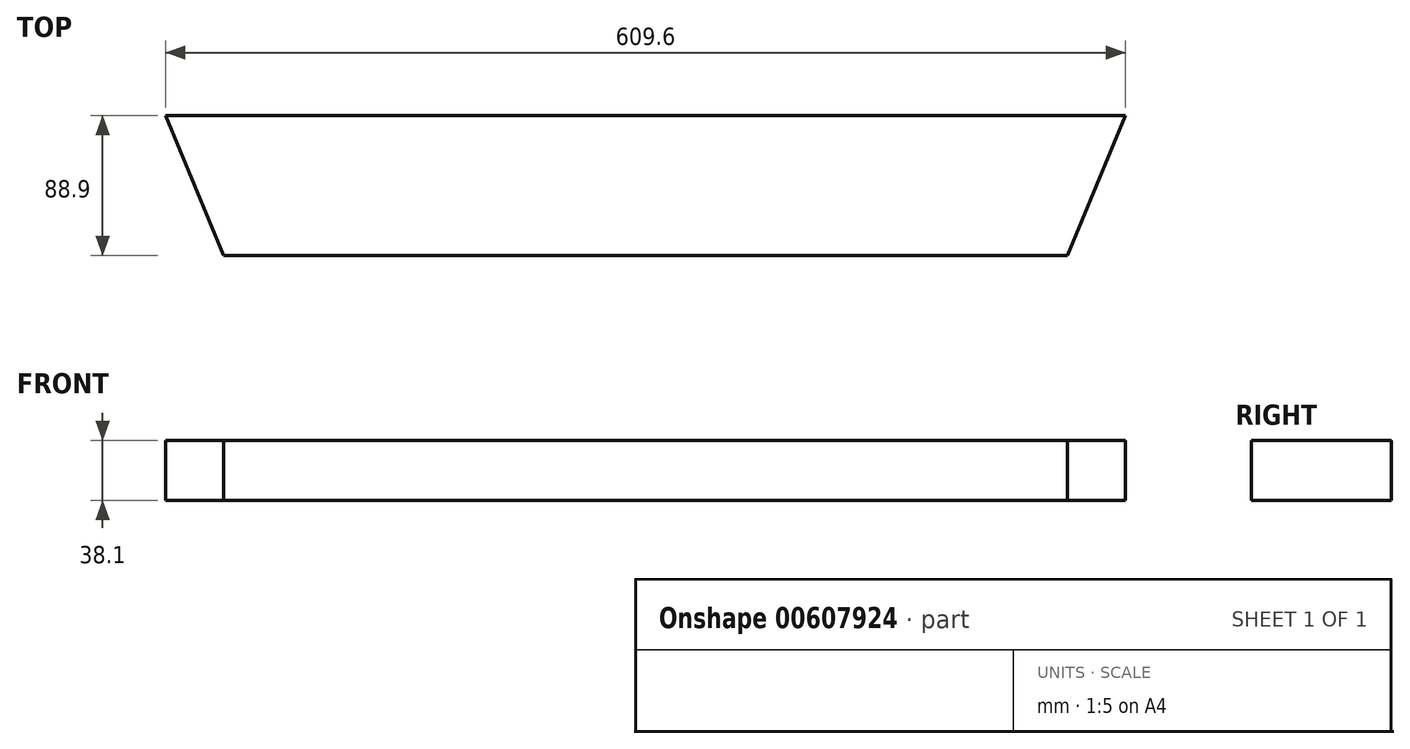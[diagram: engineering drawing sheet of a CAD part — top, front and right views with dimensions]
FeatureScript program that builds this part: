
annotation { "Feature Type Name" : "Feature", "Feature Type Description" : "" }
export const myFeature = defineFeature(function(context is Context, id is Id, definition is map)
    precondition{}
    {
        {
            var Q0;
            Q0=qCreatedBy(makeId("Top.planeOp"),FACE);
            var sketch = newSketch(context, id + "F0", { "sketchPlane" : qUnion([Q0])});
            skLineSegment(sketch, "E0", {"start": v(-316.4, 47.8) * mm, "end": v(293.2, 47.8) * mm});
            skLineSegment(sketch, "E1", {"start": v(293.2, 47.8) * mm, "end": v(256.38, -41.1) * mm});
            skLineSegment(sketch, "E2", {"start": v(256.38, -41.1) * mm, "end": v(-279.57, -41.1) * mm});
            skLineSegment(sketch, "E3", {"start": v(-279.57, -41.1) * mm, "end": v(-316.4, 47.8) * mm});
            skSolve(sketch);
        }
        {
            var Q0;
            Q0=makeQuery(id+"F0.imprint","IMPRINT",FACE,{"disambiguationData":[TD([[makeQuery(id+"F0.imprint","IMPRINT",EDGE,{"derivedFrom":sQuery(id+"F0.wireOp",EDGE,"E0")}),-1.0]])]});
            extrude(context, id + "F1", {"entities" : qUnion([Q0]), "depth" : 38.1 * mm, "offsetDistance" : 25.4 * mm});
        }
    });
